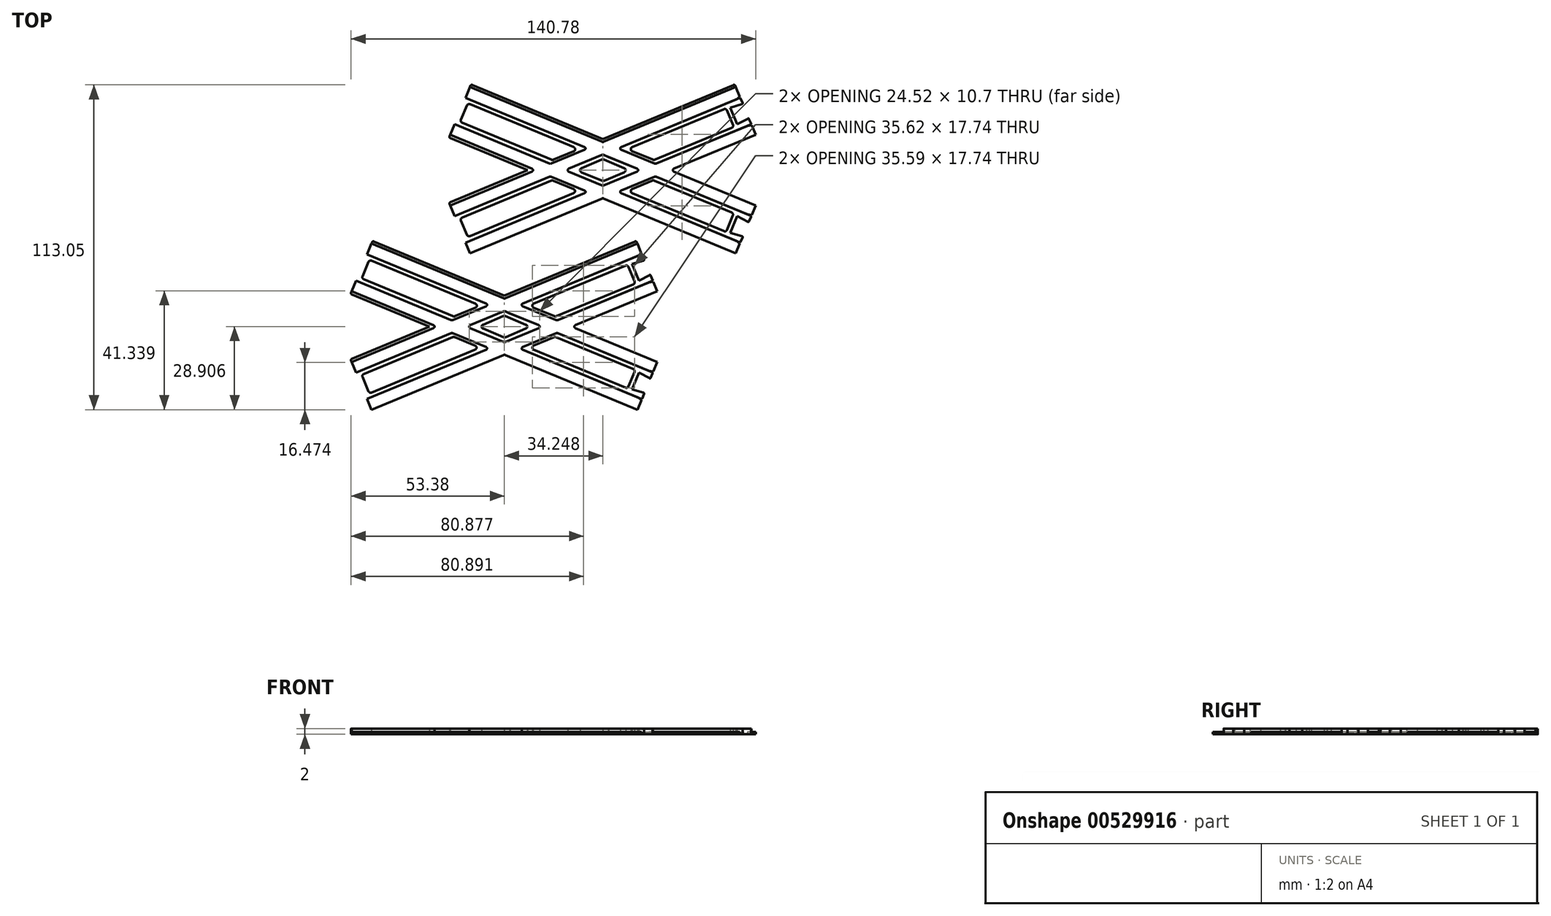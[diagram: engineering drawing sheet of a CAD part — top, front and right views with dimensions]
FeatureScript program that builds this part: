
annotation { "Feature Type Name" : "Feature", "Feature Type Description" : "" }
export const myFeature = defineFeature(function(context is Context, id is Id, definition is map)
    precondition{}
    {
        {
            var Q0;
            Q0=qCreatedBy(makeId("Top.planeOp"),FACE);
            var sketch = newSketch(context, id + "F0", { "sketchPlane" : qUnion([Q0])});
            skLineSegment(sketch, "E0.bottom", {"start": v(-69.8, -34.46) * mm, "end": v(-42.86, -23.3) * mm});
            skLineSegment(sketch, "E0.top", {"start": v(-62.15, -52.94) * mm, "end": v(-16.73, -34.13) * mm});
            skLineSegment(sketch, "E0.left", {"start": v(-70.07, -35.12) * mm, "end": v(-67.43, -41.5) * mm});
            skLineSegment(sketch, "E0.right", {"start": v(29.34, 6.06) * mm, "end": v(30.9, 2.27) * mm});
            skLineSegment(sketch, "E1.bottom", {"start": v(-69.88, -35.58) * mm, "end": v(-41.36, -23.77) * mm});
            skLineSegment(sketch, "E1.left", {"start": v(-69.88, -35.58) * mm, "end": v(-70.07, -35.12) * mm});
            skLineSegment(sketch, "E1.right", {"start": v(29.53, 5.6) * mm, "end": v(29.34, 6.06) * mm});
            skLineSegment(sketch, "E2.top", {"start": v(-63, -52.2) * mm, "end": v(-17.02, -33.16) * mm});
            skLineSegment(sketch, "E2.left", {"start": v(-62.8, -52.67) * mm, "end": v(-63, -52.2) * mm});
            skLineSegment(sketch, "E2.right", {"start": v(36.61, -11.5) * mm, "end": v(36.42, -11.03) * mm});
            skLineSegment(sketch, "E3.top", {"start": v(-68.35, -39.27) * mm, "end": v(-35.3, -25.59) * mm});
            skLineSegment(sketch, "E3.left", {"start": v(-69.88, -35.58) * mm, "end": v(-68.35, -39.27) * mm});
            skLineSegment(sketch, "E3.right", {"start": v(29.53, 5.6) * mm, "end": v(30.9, 2.27) * mm});
            skLineSegment(sketch, "E4.top", {"start": v(-64.52, -48.51) * mm, "end": v(-23.07, -31.34) * mm});
            skLineSegment(sketch, "E4.left", {"start": v(-63, -52.2) * mm, "end": v(-64.52, -48.51) * mm});
            skLineSegment(sketch, "E4.right", {"start": v(36.42, -11.03) * mm, "end": v(35.04, -7.7) * mm});
            skLineSegment(sketch, "E5", {"start": v(-69.59, -45.2) * mm, "end": v(-70.58, -45.07) * mm});
            skLineSegment(sketch, "E6", {"start": v(-70.58, -45.07) * mm, "end": v(-71.45, -42.97) * mm});
            skLineSegment(sketch, "E7", {"start": v(-71.29, -42.63) * mm, "end": v(-67.43, -41.5) * mm});
            skLineSegment(sketch, "E8.MirrorCS", {"start": v(-68.97, -48.21) * mm, "end": v(-65.44, -46.3) * mm});
            skLineSegment(sketch, "E9.MirrorCS", {"start": v(-70.2, -46) * mm, "end": v(-69.32, -48.09) * mm});
            skLineSegment(sketch, "E10.MirrorCS", {"start": v(-69.59, -45.2) * mm, "end": v(-70.2, -46) * mm});
            skLineSegment(sketch, "E11", {"start": v(27.63, -1.52) * mm, "end": v(31.68, -0.3) * mm});
            skLineSegment(sketch, "E12.MirrorCS", {"start": v(30.04, -7.34) * mm, "end": v(33.76, -5.34) * mm});
            skLineSegment(sketch, "E13", {"start": v(27.63, -1.52) * mm, "end": v(30.04, -7.34) * mm});
            skLineSegment(sketch, "E14.trimOffspring", {"start": v(35.04, -7.7) * mm, "end": v(36.61, -11.5) * mm});
            skLineSegment(sketch, "E15", {"start": v(31.16, 1.67) * mm, "end": v(31.84, 0.03) * mm});
            skLineSegment(sketch, "E16", {"start": v(34.11, -5.47) * mm, "end": v(34.89, -7.33) * mm});
            skLineSegment(sketch, "E17.trimOffspring", {"start": v(-65.44, -46.3) * mm, "end": v(-62.8, -52.67) * mm});
            skLineSegment(sketch, "E18", {"start": v(30.9, 2.27) * mm, "end": v(29.68, 1.33) * mm});
            skLineSegment(sketch, "E19", {"start": v(35.04, -7.7) * mm, "end": v(33.5, -7.9) * mm});
            skLineSegment(sketch, "E20.bottom", {"start": v(-65.7, -39.8) * mm, "end": v(-34.75, -26.98) * mm});
            skLineSegment(sketch, "E20.top", {"start": v(-63.02, -46.26) * mm, "end": v(-26.9, -31.3) * mm});
            skLineSegment(sketch, "E20.left", {"start": v(-66.1, -40.78) * mm, "end": v(-64, -45.86) * mm});
            skLineSegment(sketch, "E20.right", {"start": v(26.4, -2.46) * mm, "end": v(28.53, -7.61) * mm});
            skLineSegment(sketch, "E21.bottom", {"start": v(-62.15, 6.33) * mm, "end": v(-16.73, -12.48) * mm});
            skLineSegment(sketch, "E21.top", {"start": v(-69.8, -12.15) * mm, "end": v(-42.86, -23.3) * mm});
            skLineSegment(sketch, "E21.left", {"start": v(-62.8, 6.06) * mm, "end": v(-65.44, -0.31) * mm});
            skLineSegment(sketch, "E21.right", {"start": v(36.61, -35.12) * mm, "end": v(35.04, -38.9) * mm});
            skLineSegment(sketch, "E22.bottom", {"start": v(-63, 5.6) * mm, "end": v(-17.02, -13.44) * mm});
            skLineSegment(sketch, "E22.left", {"start": v(-63, 5.6) * mm, "end": v(-62.8, 6.06) * mm});
            skLineSegment(sketch, "E22.right", {"start": v(36.42, -35.58) * mm, "end": v(36.61, -35.12) * mm});
            skLineSegment(sketch, "E23.top", {"start": v(-69.88, -11.03) * mm, "end": v(-41.36, -22.84) * mm});
            skLineSegment(sketch, "E23.left", {"start": v(-70.07, -11.5) * mm, "end": v(-69.88, -11.03) * mm});
            skLineSegment(sketch, "E23.right", {"start": v(29.34, -52.67) * mm, "end": v(29.53, -52.2) * mm});
            skLineSegment(sketch, "E24.top", {"start": v(-64.52, 1.9) * mm, "end": v(-23.07, -15.27) * mm});
            skLineSegment(sketch, "E24.left", {"start": v(-63, 5.6) * mm, "end": v(-64.52, 1.9) * mm});
            skLineSegment(sketch, "E24.right", {"start": v(36.42, -35.58) * mm, "end": v(35.04, -38.9) * mm});
            skLineSegment(sketch, "E25.top", {"start": v(-68.35, -7.33) * mm, "end": v(-35.3, -21.02) * mm});
            skLineSegment(sketch, "E25.left", {"start": v(-69.88, -11.03) * mm, "end": v(-68.35, -7.33) * mm});
            skLineSegment(sketch, "E25.right", {"start": v(29.53, -52.2) * mm, "end": v(30.9, -48.88) * mm});
            skLineSegment(sketch, "E26", {"start": v(-69.59, -1.41) * mm, "end": v(-70.2, -0.62) * mm});
            skLineSegment(sketch, "E27", {"start": v(-70.2, -0.62) * mm, "end": v(-69.32, 1.48) * mm});
            skLineSegment(sketch, "E28", {"start": v(-68.97, 1.6) * mm, "end": v(-65.44, -0.31) * mm});
            skLineSegment(sketch, "E29.MirrorCS", {"start": v(-71.29, -3.98) * mm, "end": v(-67.43, -5.12) * mm});
            skLineSegment(sketch, "E30.MirrorCS", {"start": v(-70.58, -1.54) * mm, "end": v(-71.45, -3.64) * mm});
            skLineSegment(sketch, "E31.MirrorCS", {"start": v(-69.59, -1.41) * mm, "end": v(-70.58, -1.54) * mm});
            skLineSegment(sketch, "E32", {"start": v(30.04, -39.27) * mm, "end": v(33.76, -41.27) * mm});
            skLineSegment(sketch, "E33.MirrorCS", {"start": v(27.63, -45.09) * mm, "end": v(31.68, -46.3) * mm});
            skLineSegment(sketch, "E34", {"start": v(30.04, -39.27) * mm, "end": v(27.63, -45.09) * mm});
            skLineSegment(sketch, "E35.trimOffspring", {"start": v(30.9, -48.88) * mm, "end": v(29.34, -52.67) * mm});
            skLineSegment(sketch, "E36", {"start": v(34.8, -39.5) * mm, "end": v(34.11, -41.14) * mm});
            skLineSegment(sketch, "E37", {"start": v(31.84, -46.64) * mm, "end": v(31.16, -48.28) * mm});
            skLineSegment(sketch, "E38.trimOffspring", {"start": v(-67.43, -5.12) * mm, "end": v(-70.07, -11.5) * mm});
            skLineSegment(sketch, "E39", {"start": v(35.04, -38.9) * mm, "end": v(33.5, -38.7) * mm});
            skLineSegment(sketch, "E40", {"start": v(30.9, -48.88) * mm, "end": v(29.68, -47.94) * mm});
            skLineSegment(sketch, "E41.bottom", {"start": v(-63.02, -0.34) * mm, "end": v(-26.8, -15.34) * mm});
            skLineSegment(sketch, "E41.top", {"start": v(-65.7, -6.81) * mm, "end": v(-34.66, -19.67) * mm});
            skLineSegment(sketch, "E41.left", {"start": v(-64, -0.75) * mm, "end": v(-66.1, -5.83) * mm});
            skLineSegment(sketch, "E41.right", {"start": v(28.5, -39.06) * mm, "end": v(26.4, -44.15) * mm});
            skLineSegment(sketch, "E42", {"start": v(-6.56, -16.7) * mm, "end": v(0.62, -19.67) * mm});
            skLineSegment(sketch, "E43", {"start": v(-18.62, -27.88) * mm, "end": v(-18.64, -27.92) * mm});
            skPoint(sketch, "E44", {"position": v(-18.64, -18.68) * mm});
            skLineSegment(sketch, "E45.trimOffspring", {"start": v(-16.73, -34.13) * mm, "end": v(28.69, -52.94) * mm});
            skLineSegment(sketch, "E46.trimOffspring", {"start": v(-16.44, -33.16) * mm, "end": v(29.53, -52.2) * mm});
            skLineSegment(sketch, "E47.trimOffspring", {"start": v(-10.39, -31.34) * mm, "end": v(30.83, -48.42) * mm});
            skLineSegment(sketch, "E48.trimOffspring", {"start": v(-6.56, -31.3) * mm, "end": v(25.42, -44.55) * mm});
            skLineSegment(sketch, "E49.trimOffspring", {"start": v(-34.37, -26.82) * mm, "end": v(-26.9, -29.92) * mm});
            skLineSegment(sketch, "E50.trimOffspring", {"start": v(-34.73, -25.59) * mm, "end": v(-23.07, -30.42) * mm});
            skLineSegment(sketch, "E51.trimOffspring", {"start": v(-33.99, -26.98) * mm, "end": v(-26.9, -29.92) * mm});
            skLineSegment(sketch, "E52.trimOffspring", {"start": v(-28.68, -23.77) * mm, "end": v(-17.02, -28.6) * mm});
            skLineSegment(sketch, "E53.trimOffspring", {"start": v(-24.2, -24) * mm, "end": v(-17.02, -26.97) * mm});
            skLineSegment(sketch, "E54.trimOffspring", {"start": v(-16.35, -19.67) * mm, "end": v(-9.26, -22.61) * mm});
            skLineSegment(sketch, "E55.trimOffspring", {"start": v(-16.44, -18.01) * mm, "end": v(-4.78, -22.84) * mm});
            skLineSegment(sketch, "E56.trimOffspring", {"start": v(-23.92, -16.54) * mm, "end": v(-23.07, -16.19) * mm});
            skLineSegment(sketch, "E57.trimOffspring", {"start": v(-18.69, -18.7) * mm, "end": v(-17.02, -18.01) * mm});
            skLineSegment(sketch, "E58.trimOffspring", {"start": v(-14.84, -18.73) * mm, "end": v(-14.77, -18.7) * mm});
            skLineSegment(sketch, "E59.trimOffspring", {"start": v(-5.62, -24.12) * mm, "end": v(-4.78, -23.77) * mm});
            skLineSegment(sketch, "E60.trimOffspring", {"start": v(-0.4, -26.28) * mm, "end": v(1.28, -25.59) * mm});
            skLineSegment(sketch, "E61.trimOffspring", {"start": v(-14.82, -18.68) * mm, "end": v(-14.84, -18.73) * mm});
            skLineSegment(sketch, "E62.trimOffspring", {"start": v(-6.56, -16.7) * mm, "end": v(1, -19.83) * mm});
            skLineSegment(sketch, "E63.trimOffspring", {"start": v(-10.39, -16.19) * mm, "end": v(1.28, -21.02) * mm});
            skLineSegment(sketch, "E64.trimOffspring", {"start": v(1.2, -26.94) * mm, "end": v(28.1, -38.08) * mm});
            skLineSegment(sketch, "E65.trimOffspring", {"start": v(1.85, -25.59) * mm, "end": v(34.66, -39.18) * mm});
            skLineSegment(sketch, "E66.trimOffspring", {"start": v(7.9, -23.77) * mm, "end": v(36.42, -35.58) * mm});
            skLineSegment(sketch, "E67.trimOffspring", {"start": v(9.4, -23.3) * mm, "end": v(36.34, -34.46) * mm});
            skLineSegment(sketch, "E68.trimOffspring", {"start": v(-34.73, -21.02) * mm, "end": v(-33.06, -20.33) * mm});
            skLineSegment(sketch, "E69.trimOffspring", {"start": v(-28.68, -22.84) * mm, "end": v(-27.84, -22.5) * mm});
            skLineSegment(sketch, "E70.trimOffspring", {"start": v(-16.73, -12.48) * mm, "end": v(28.69, 6.33) * mm});
            skLineSegment(sketch, "E71.trimOffspring", {"start": v(-16.44, -13.44) * mm, "end": v(29.53, 5.6) * mm});
            skLineSegment(sketch, "E72.trimOffspring", {"start": v(-10.39, -15.27) * mm, "end": v(30.83, 1.8) * mm});
            skLineSegment(sketch, "E73.trimOffspring", {"start": v(-6.56, -15.3) * mm, "end": v(25.42, -2.06) * mm});
            skLineSegment(sketch, "E74.trimOffspring", {"start": v(-16.44, -28.6) * mm, "end": v(-14.77, -27.9) * mm});
            skLineSegment(sketch, "E75.trimOffspring", {"start": v(1.39, -19.67) * mm, "end": v(28.13, -8.6) * mm});
            skLineSegment(sketch, "E76.trimOffspring", {"start": v(1.85, -21.02) * mm, "end": v(34.89, -7.33) * mm});
            skLineSegment(sketch, "E77.trimOffspring", {"start": v(7.9, -22.84) * mm, "end": v(36.42, -11.03) * mm});
            skLineSegment(sketch, "E78.trimOffspring", {"start": v(9.4, -23.3) * mm, "end": v(36.34, -12.15) * mm});
            skLineSegment(sketch, "E79.trimOffspring", {"start": v(-10.39, -30.42) * mm, "end": v(-9.54, -30.07) * mm});
            skLineSegment(sketch, "E80", {"start": v(-33.06, -20.33) * mm, "end": v(-23.92, -16.54) * mm});
            skLineSegment(sketch, "E81", {"start": v(-27.84, -22.5) * mm, "end": v(-18.64, -18.68) * mm});
            skLineSegment(sketch, "E82", {"start": v(-14.77, -27.9) * mm, "end": v(-5.62, -24.12) * mm});
            skLineSegment(sketch, "E83", {"start": v(-9.54, -30.07) * mm, "end": v(-0.4, -26.28) * mm});
            skLineSegment(sketch, "E84", {"start": v(-24.2, -22.61) * mm, "end": v(-17.11, -19.67) * mm});
            skLineSegment(sketch, "E85", {"start": v(-16.24, -26.97) * mm, "end": v(-9.25, -24) * mm});
            skLineSegment(sketch, "E86", {"start": v(-26.8, -16.73) * mm, "end": v(-33.9, -19.67) * mm});
            skLineSegment(sketch, "E87", {"start": v(-6.57, -29.92) * mm, "end": v(0.42, -26.94) * mm});
            skPoint(sketch, "E88.visualSharp", {"position": v(-40.25, -23.3) * mm});
            skArc(sketch, "E88.filletArc", {"start": v(-41.36, -23.77) * mm, "mid": v(-41.05, -23.3) * mm, "end": v(-41.36, -22.84) * mm});
            skPoint(sketch, "E89.visualSharp", {"position": v(-29.8, -23.3) * mm});
            skArc(sketch, "E89.filletArc", {"start": v(-28.68, -22.84) * mm, "mid": v(-28.99, -23.3) * mm, "end": v(-28.68, -23.77) * mm});
            skPoint(sketch, "E90.visualSharp", {"position": v(-21.96, -15.73) * mm});
            skArc(sketch, "E90.filletArc", {"start": v(-23.07, -16.19) * mm, "mid": v(-22.76, -15.73) * mm, "end": v(-23.07, -15.27) * mm});
            skPoint(sketch, "E91.visualSharp", {"position": v(-3.66, -23.3) * mm});
            skArc(sketch, "E91.filletArc", {"start": v(-4.78, -23.77) * mm, "mid": v(-4.47, -23.3) * mm, "end": v(-4.78, -22.84) * mm});
            skPoint(sketch, "E92.visualSharp", {"position": v(-11.5, -15.73) * mm});
            skArc(sketch, "E92.filletArc", {"start": v(-10.39, -15.27) * mm, "mid": v(-10.7, -15.73) * mm, "end": v(-10.39, -16.19) * mm});
            skPoint(sketch, "E93.visualSharp", {"position": v(6.79, -23.3) * mm});
            skArc(sketch, "E93.filletArc", {"start": v(7.9, -22.84) * mm, "mid": v(7.6, -23.3) * mm, "end": v(7.9, -23.77) * mm});
            skPoint(sketch, "E94.visualSharp", {"position": v(-11.5, -30.88) * mm});
            skArc(sketch, "E94.filletArc", {"start": v(-10.39, -30.42) * mm, "mid": v(-10.7, -30.88) * mm, "end": v(-10.39, -31.34) * mm});
            skPoint(sketch, "E95.visualSharp", {"position": v(-21.96, -30.88) * mm});
            skArc(sketch, "E95.filletArc", {"start": v(-23.07, -31.34) * mm, "mid": v(-22.76, -30.88) * mm, "end": v(-23.07, -30.42) * mm});
            skPoint(sketch, "E96.visualSharp", {"position": v(-16.73, -33.05) * mm});
            skArc(sketch, "E96.filletArc", {"start": v(-16.44, -33.16) * mm, "mid": v(-16.73, -33.1) * mm, "end": v(-17.02, -33.16) * mm});
            skPoint(sketch, "E97.visualSharp", {"position": v(1.56, -21.14) * mm});
            skArc(sketch, "E97.filletArc", {"start": v(1.28, -21.02) * mm, "mid": v(1.56, -21.08) * mm, "end": v(1.85, -21.02) * mm});
            skPoint(sketch, "E98.visualSharp", {"position": v(1.56, -25.47) * mm});
            skArc(sketch, "E98.filletArc", {"start": v(1.85, -25.59) * mm, "mid": v(1.56, -25.53) * mm, "end": v(1.28, -25.59) * mm});
            skPoint(sketch, "E99.visualSharp", {"position": v(-16.73, -28.72) * mm});
            skArc(sketch, "E99.filletArc", {"start": v(-17.02, -28.6) * mm, "mid": v(-16.73, -28.65) * mm, "end": v(-16.44, -28.6) * mm});
            skPoint(sketch, "E100.visualSharp", {"position": v(-16.73, -17.9) * mm});
            skArc(sketch, "E100.filletArc", {"start": v(-16.44, -18.01) * mm, "mid": v(-16.73, -17.95) * mm, "end": v(-17.02, -18.01) * mm});
            skPoint(sketch, "E101.visualSharp", {"position": v(-16.73, -13.56) * mm});
            skArc(sketch, "E101.filletArc", {"start": v(-17.02, -13.44) * mm, "mid": v(-16.73, -13.5) * mm, "end": v(-16.44, -13.44) * mm});
            skPoint(sketch, "E102.visualSharp", {"position": v(-35.02, -21.14) * mm});
            skArc(sketch, "E102.filletArc", {"start": v(-35.3, -21.02) * mm, "mid": v(-35.02, -21.08) * mm, "end": v(-34.73, -21.02) * mm});
            skPoint(sketch, "E103.visualSharp", {"position": v(-35.02, -25.47) * mm});
            skArc(sketch, "E103.filletArc", {"start": v(-34.73, -25.59) * mm, "mid": v(-35.02, -25.53) * mm, "end": v(-35.3, -25.59) * mm});
            skPoint(sketch, "E104.visualSharp", {"position": v(-70.26, -11.95) * mm});
            skArc(sketch, "E104.filletArc", {"start": v(-70.07, -11.5) * mm, "mid": v(-70.07, -11.87) * mm, "end": v(-69.8, -12.15) * mm});
            skPoint(sketch, "E105.visualSharp", {"position": v(-62.6, 6.52) * mm});
            skArc(sketch, "E105.filletArc", {"start": v(-62.15, 6.33) * mm, "mid": v(-62.53, 6.33) * mm, "end": v(-62.8, 6.06) * mm});
            skPoint(sketch, "E106.visualSharp", {"position": v(-69.22, 1.74) * mm});
            skArc(sketch, "E106.filletArc", {"start": v(-68.97, 1.6) * mm, "mid": v(-69.18, 1.62) * mm, "end": v(-69.32, 1.48) * mm});
            skPoint(sketch, "E107.visualSharp", {"position": v(-71.55, -3.9) * mm});
            skArc(sketch, "E107.filletArc", {"start": v(-71.45, -3.64) * mm, "mid": v(-71.44, -3.84) * mm, "end": v(-71.29, -3.98) * mm});
            skPoint(sketch, "E108.visualSharp", {"position": v(-66.39, -6.52) * mm});
            skArc(sketch, "E108.filletArc", {"start": v(-66.1, -5.83) * mm, "mid": v(-66.1, -6.4) * mm, "end": v(-65.7, -6.81) * mm});
            skPoint(sketch, "E109.visualSharp", {"position": v(-63.7, -0.06) * mm});
            skArc(sketch, "E109.filletArc", {"start": v(-63.02, -0.34) * mm, "mid": v(-63.6, -0.34) * mm, "end": v(-64, -0.75) * mm});
            skPoint(sketch, "E110.visualSharp", {"position": v(31.94, -0.22) * mm});
            skArc(sketch, "E110.filletArc", {"start": v(31.68, -0.3) * mm, "mid": v(31.83, -0.17) * mm, "end": v(31.84, 0.03) * mm});
            skPoint(sketch, "E111.visualSharp", {"position": v(34, -5.2) * mm});
            skArc(sketch, "E111.filletArc", {"start": v(34.11, -5.47) * mm, "mid": v(33.97, -5.33) * mm, "end": v(33.76, -5.34) * mm});
            skPoint(sketch, "E112.visualSharp", {"position": v(29.15, 6.52) * mm});
            skArc(sketch, "E112.filletArc", {"start": v(29.34, 6.06) * mm, "mid": v(29.07, 6.33) * mm, "end": v(28.69, 6.33) * mm});
            skPoint(sketch, "E113.visualSharp", {"position": v(36.8, -11.95) * mm});
            skArc(sketch, "E113.filletArc", {"start": v(36.34, -12.15) * mm, "mid": v(36.61, -11.87) * mm, "end": v(36.61, -11.5) * mm});
            skPoint(sketch, "E114.visualSharp", {"position": v(36.8, -34.65) * mm});
            skArc(sketch, "E114.filletArc", {"start": v(36.61, -35.12) * mm, "mid": v(36.61, -34.73) * mm, "end": v(36.34, -34.46) * mm});
            skPoint(sketch, "E115.visualSharp", {"position": v(29.15, -53.13) * mm});
            skArc(sketch, "E115.filletArc", {"start": v(28.69, -52.94) * mm, "mid": v(29.07, -52.94) * mm, "end": v(29.34, -52.67) * mm});
            skPoint(sketch, "E116.visualSharp", {"position": v(31.06, -48.51) * mm});
            skArc(sketch, "E116.filletArc", {"start": v(30.83, -48.42) * mm, "mid": v(31.02, -48.42) * mm, "end": v(31.16, -48.28) * mm});
            skPoint(sketch, "E117.visualSharp", {"position": v(34.89, -39.27) * mm});
            skArc(sketch, "E117.filletArc", {"start": v(34.8, -39.5) * mm, "mid": v(34.8, -39.31) * mm, "end": v(34.66, -39.18) * mm});
            skPoint(sketch, "E118.visualSharp", {"position": v(34, -41.4) * mm});
            skArc(sketch, "E118.filletArc", {"start": v(33.76, -41.27) * mm, "mid": v(33.97, -41.28) * mm, "end": v(34.11, -41.14) * mm});
            skPoint(sketch, "E119.visualSharp", {"position": v(31.94, -46.39) * mm});
            skArc(sketch, "E119.filletArc", {"start": v(31.84, -46.64) * mm, "mid": v(31.83, -46.44) * mm, "end": v(31.68, -46.3) * mm});
            skPoint(sketch, "E120.visualSharp", {"position": v(26.11, -44.84) * mm});
            skArc(sketch, "E120.filletArc", {"start": v(25.42, -44.55) * mm, "mid": v(26, -44.55) * mm, "end": v(26.4, -44.15) * mm});
            skPoint(sketch, "E121.visualSharp", {"position": v(28.8, -38.37) * mm});
            skArc(sketch, "E121.filletArc", {"start": v(28.5, -39.06) * mm, "mid": v(28.5, -38.49) * mm, "end": v(28.1, -38.08) * mm});
            skPoint(sketch, "E122.visualSharp", {"position": v(-8.21, -30.62) * mm});
            skArc(sketch, "E122.filletArc", {"start": v(-6.57, -29.92) * mm, "mid": v(-7.03, -30.61) * mm, "end": v(-6.56, -31.3) * mm});
            skPoint(sketch, "E123.visualSharp", {"position": v(0.8, -26.78) * mm});
            skArc(sketch, "E123.filletArc", {"start": v(1.2, -26.94) * mm, "mid": v(0.8, -26.86) * mm, "end": v(0.42, -26.94) * mm});
            skPoint(sketch, "E124.visualSharp", {"position": v(-25.88, -23.3) * mm});
            skArc(sketch, "E124.filletArc", {"start": v(-24.2, -22.61) * mm, "mid": v(-24.67, -23.3) * mm, "end": v(-24.2, -24) * mm});
            skPoint(sketch, "E125.visualSharp", {"position": v(-7.6, -23.3) * mm});
            skArc(sketch, "E125.filletArc", {"start": v(-9.25, -24) * mm, "mid": v(-8.8, -23.3) * mm, "end": v(-9.26, -22.61) * mm});
            skPoint(sketch, "E126.visualSharp", {"position": v(-8.24, -16) * mm});
            skArc(sketch, "E126.filletArc", {"start": v(-6.56, -15.3) * mm, "mid": v(-7.03, -16) * mm, "end": v(-6.56, -16.7) * mm});
            skPoint(sketch, "E127.visualSharp", {"position": v(-25.22, -30.6) * mm});
            skArc(sketch, "E127.filletArc", {"start": v(-26.9, -31.3) * mm, "mid": v(-26.43, -30.6) * mm, "end": v(-26.9, -29.92) * mm});
            skPoint(sketch, "E128.visualSharp", {"position": v(-63.7, -46.55) * mm});
            skArc(sketch, "E128.filletArc", {"start": v(-64, -45.86) * mm, "mid": v(-63.6, -46.26) * mm, "end": v(-63.02, -46.26) * mm});
            skPoint(sketch, "E129.visualSharp", {"position": v(-66.39, -40.08) * mm});
            skArc(sketch, "E129.filletArc", {"start": v(-65.7, -39.8) * mm, "mid": v(-66.1, -40.2) * mm, "end": v(-66.1, -40.78) * mm});
            skPoint(sketch, "E130.visualSharp", {"position": v(-71.55, -42.71) * mm});
            skArc(sketch, "E130.filletArc", {"start": v(-71.29, -42.63) * mm, "mid": v(-71.44, -42.76) * mm, "end": v(-71.45, -42.97) * mm});
            skPoint(sketch, "E131.visualSharp", {"position": v(-69.22, -48.35) * mm});
            skArc(sketch, "E131.filletArc", {"start": v(-69.32, -48.09) * mm, "mid": v(-69.18, -48.23) * mm, "end": v(-68.97, -48.21) * mm});
            skPoint(sketch, "E132.visualSharp", {"position": v(-70.26, -34.65) * mm});
            skArc(sketch, "E132.filletArc", {"start": v(-69.8, -34.46) * mm, "mid": v(-70.07, -34.73) * mm, "end": v(-70.07, -35.12) * mm});
            skPoint(sketch, "E133.visualSharp", {"position": v(-62.6, -53.13) * mm});
            skArc(sketch, "E133.filletArc", {"start": v(-62.8, -52.67) * mm, "mid": v(-62.53, -52.94) * mm, "end": v(-62.15, -52.94) * mm});
            skPoint(sketch, "E134.visualSharp", {"position": v(-34.37, -26.82) * mm});
            skArc(sketch, "E134.filletArc", {"start": v(-33.99, -26.98) * mm, "mid": v(-34.37, -26.9) * mm, "end": v(-34.75, -26.98) * mm});
            skPoint(sketch, "E135.visualSharp", {"position": v(-16.63, -27.13) * mm});
            skArc(sketch, "E135.filletArc", {"start": v(-17.02, -26.97) * mm, "mid": v(-16.63, -27.05) * mm, "end": v(-16.24, -26.97) * mm});
            skPoint(sketch, "E136.visualSharp", {"position": v(-16.73, -19.52) * mm});
            skArc(sketch, "E136.filletArc", {"start": v(-16.35, -19.67) * mm, "mid": v(-16.73, -19.6) * mm, "end": v(-17.11, -19.67) * mm});
            skPoint(sketch, "E137.visualSharp", {"position": v(1, -19.83) * mm});
            skArc(sketch, "E137.filletArc", {"start": v(0.62, -19.67) * mm, "mid": v(1, -19.74) * mm, "end": v(1.39, -19.67) * mm});
            skPoint(sketch, "E138.visualSharp", {"position": v(26.11, -1.77) * mm});
            skArc(sketch, "E138.filletArc", {"start": v(26.4, -2.46) * mm, "mid": v(26, -2.06) * mm, "end": v(25.42, -2.06) * mm});
            skPoint(sketch, "E139.visualSharp", {"position": v(28.82, -8.3) * mm});
            skArc(sketch, "E139.filletArc", {"start": v(28.13, -8.6) * mm, "mid": v(28.53, -8.19) * mm, "end": v(28.53, -7.61) * mm});
            skPoint(sketch, "E140.visualSharp", {"position": v(-34.27, -19.83) * mm});
            skArc(sketch, "E140.filletArc", {"start": v(-34.66, -19.67) * mm, "mid": v(-34.27, -19.74) * mm, "end": v(-33.9, -19.67) * mm});
            skPoint(sketch, "E141.visualSharp", {"position": v(-25.13, -16.04) * mm});
            skArc(sketch, "E141.filletArc", {"start": v(-26.8, -16.73) * mm, "mid": v(-26.34, -16.04) * mm, "end": v(-26.8, -15.34) * mm});
            skPoint(sketch, "E142.visualSharp", {"position": v(31.06, 1.9) * mm});
            skArc(sketch, "E142.filletArc", {"start": v(31.16, 1.67) * mm, "mid": v(31.02, 1.8) * mm, "end": v(30.83, 1.8) * mm});
            skLineSegment(sketch, "E143.bottom", {"start": v(-35.55, 20.01) * mm, "end": v(-8.61, 31.17) * mm});
            skLineSegment(sketch, "E143.top", {"start": v(-27.9, 1.53) * mm, "end": v(17.52, 20.35) * mm});
            skLineSegment(sketch, "E143.left", {"start": v(-35.82, 19.36) * mm, "end": v(-33.18, 12.98) * mm});
            skLineSegment(sketch, "E143.right", {"start": v(63.59, 60.53) * mm, "end": v(65.16, 56.75) * mm});
            skLineSegment(sketch, "E144.bottom", {"start": v(-35.63, 18.9) * mm, "end": v(-7.11, 30.7) * mm});
            skLineSegment(sketch, "E144.left", {"start": v(-35.63, 18.9) * mm, "end": v(-35.82, 19.36) * mm});
            skLineSegment(sketch, "E144.right", {"start": v(63.78, 60.07) * mm, "end": v(63.59, 60.53) * mm});
            skLineSegment(sketch, "E145.top", {"start": v(-28.74, 2.27) * mm, "end": v(17.23, 21.3) * mm});
            skLineSegment(sketch, "E145.left", {"start": v(-28.55, 1.8) * mm, "end": v(-28.74, 2.27) * mm});
            skLineSegment(sketch, "E145.right", {"start": v(70.86, 42.98) * mm, "end": v(70.67, 43.44) * mm});
            skLineSegment(sketch, "E146.top", {"start": v(-34.1, 15.2) * mm, "end": v(-1.06, 28.89) * mm});
            skLineSegment(sketch, "E146.left", {"start": v(-35.63, 18.9) * mm, "end": v(-34.1, 15.2) * mm});
            skLineSegment(sketch, "E146.right", {"start": v(63.78, 60.07) * mm, "end": v(65.16, 56.75) * mm});
            skLineSegment(sketch, "E147.top", {"start": v(-30.27, 5.96) * mm, "end": v(11.18, 23.13) * mm});
            skLineSegment(sketch, "E147.left", {"start": v(-28.74, 2.27) * mm, "end": v(-30.27, 5.96) * mm});
            skLineSegment(sketch, "E147.right", {"start": v(70.67, 43.44) * mm, "end": v(69.29, 46.77) * mm});
            skLineSegment(sketch, "E148", {"start": v(-35.34, 9.28) * mm, "end": v(-36.33, 9.4) * mm});
            skLineSegment(sketch, "E149", {"start": v(-36.33, 9.4) * mm, "end": v(-37.2, 11.5) * mm});
            skLineSegment(sketch, "E150", {"start": v(-37.04, 11.84) * mm, "end": v(-33.18, 12.98) * mm});
            skLineSegment(sketch, "E151.MirrorCS", {"start": v(-34.73, 6.26) * mm, "end": v(-31.2, 8.18) * mm});
            skLineSegment(sketch, "E152.MirrorCS", {"start": v(-35.95, 8.48) * mm, "end": v(-35.08, 6.38) * mm});
            skLineSegment(sketch, "E153.MirrorCS", {"start": v(-35.34, 9.28) * mm, "end": v(-35.95, 8.48) * mm});
            skLineSegment(sketch, "E154", {"start": v(61.88, 52.95) * mm, "end": v(65.93, 54.17) * mm});
            skLineSegment(sketch, "E155.MirrorCS", {"start": v(64.3, 47.13) * mm, "end": v(68.01, 49.13) * mm});
            skLineSegment(sketch, "E156", {"start": v(61.88, 52.95) * mm, "end": v(64.3, 47.13) * mm});
            skLineSegment(sketch, "E157.trimOffspring", {"start": v(69.29, 46.77) * mm, "end": v(70.86, 42.98) * mm});
            skLineSegment(sketch, "E158", {"start": v(65.4, 56.15) * mm, "end": v(66.08, 54.5) * mm});
            skLineSegment(sketch, "E159", {"start": v(68.36, 49) * mm, "end": v(69.14, 47.14) * mm});
            skLineSegment(sketch, "E160.trimOffspring", {"start": v(-31.2, 8.18) * mm, "end": v(-28.55, 1.8) * mm});
            skLineSegment(sketch, "E161", {"start": v(65.16, 56.75) * mm, "end": v(63.92, 55.8) * mm});
            skLineSegment(sketch, "E162", {"start": v(69.29, 46.77) * mm, "end": v(67.75, 46.56) * mm});
            skLineSegment(sketch, "E163.bottom", {"start": v(-31.45, 14.68) * mm, "end": v(-0.5, 27.5) * mm});
            skLineSegment(sketch, "E163.top", {"start": v(-28.77, 8.2) * mm, "end": v(7.35, 23.17) * mm});
            skLineSegment(sketch, "E163.left", {"start": v(-31.85, 13.7) * mm, "end": v(-29.75, 8.61) * mm});
            skLineSegment(sketch, "E163.right", {"start": v(60.65, 52.01) * mm, "end": v(62.78, 46.86) * mm});
            skLineSegment(sketch, "E164.bottom", {"start": v(-27.9, 60.8) * mm, "end": v(17.52, 42) * mm});
            skLineSegment(sketch, "E164.top", {"start": v(-35.55, 42.33) * mm, "end": v(-8.61, 31.17) * mm});
            skLineSegment(sketch, "E164.left", {"start": v(-28.55, 60.53) * mm, "end": v(-31.2, 54.16) * mm});
            skLineSegment(sketch, "E164.right", {"start": v(70.86, 19.36) * mm, "end": v(69.3, 15.57) * mm});
            skLineSegment(sketch, "E165.bottom", {"start": v(-28.74, 60.07) * mm, "end": v(17.23, 41.03) * mm});
            skLineSegment(sketch, "E165.left", {"start": v(-28.74, 60.07) * mm, "end": v(-28.55, 60.53) * mm});
            skLineSegment(sketch, "E165.right", {"start": v(70.67, 18.9) * mm, "end": v(70.86, 19.36) * mm});
            skLineSegment(sketch, "E166.top", {"start": v(-35.63, 43.44) * mm, "end": v(-7.11, 31.63) * mm});
            skLineSegment(sketch, "E166.left", {"start": v(-35.82, 42.98) * mm, "end": v(-35.63, 43.44) * mm});
            skLineSegment(sketch, "E166.right", {"start": v(63.59, 1.8) * mm, "end": v(63.78, 2.27) * mm});
            skLineSegment(sketch, "E167.top", {"start": v(-30.27, 56.38) * mm, "end": v(11.18, 39.2) * mm});
            skLineSegment(sketch, "E167.left", {"start": v(-28.74, 60.07) * mm, "end": v(-30.27, 56.38) * mm});
            skLineSegment(sketch, "E167.right", {"start": v(70.67, 18.9) * mm, "end": v(69.3, 15.57) * mm});
            skLineSegment(sketch, "E168.top", {"start": v(-34.1, 47.14) * mm, "end": v(-1.06, 33.45) * mm});
            skLineSegment(sketch, "E168.left", {"start": v(-35.63, 43.44) * mm, "end": v(-34.1, 47.14) * mm});
            skLineSegment(sketch, "E168.right", {"start": v(63.78, 2.27) * mm, "end": v(65.16, 5.6) * mm});
            skLineSegment(sketch, "E169", {"start": v(-35.34, 53.06) * mm, "end": v(-35.95, 53.86) * mm});
            skLineSegment(sketch, "E170", {"start": v(-35.95, 53.86) * mm, "end": v(-35.08, 55.96) * mm});
            skLineSegment(sketch, "E171", {"start": v(-34.73, 56.08) * mm, "end": v(-31.2, 54.16) * mm});
            skLineSegment(sketch, "E172.MirrorCS", {"start": v(-37.04, 50.5) * mm, "end": v(-33.18, 49.36) * mm});
            skLineSegment(sketch, "E173.MirrorCS", {"start": v(-36.33, 52.93) * mm, "end": v(-37.2, 50.83) * mm});
            skLineSegment(sketch, "E174.MirrorCS", {"start": v(-35.34, 53.06) * mm, "end": v(-36.33, 52.93) * mm});
            skLineSegment(sketch, "E175", {"start": v(64.3, 15.2) * mm, "end": v(68.01, 13.2) * mm});
            skLineSegment(sketch, "E176.MirrorCS", {"start": v(61.88, 9.38) * mm, "end": v(65.93, 8.17) * mm});
            skLineSegment(sketch, "E177", {"start": v(64.3, 15.2) * mm, "end": v(61.88, 9.38) * mm});
            skLineSegment(sketch, "E178.trimOffspring", {"start": v(65.16, 5.6) * mm, "end": v(63.59, 1.8) * mm});
            skLineSegment(sketch, "E179", {"start": v(69.04, 14.97) * mm, "end": v(68.36, 13.33) * mm});
            skLineSegment(sketch, "E180", {"start": v(66.08, 7.83) * mm, "end": v(65.4, 6.2) * mm});
            skLineSegment(sketch, "E181.trimOffspring", {"start": v(-33.18, 49.36) * mm, "end": v(-35.82, 42.98) * mm});
            skLineSegment(sketch, "E182", {"start": v(69.3, 15.57) * mm, "end": v(67.75, 15.77) * mm});
            skLineSegment(sketch, "E183", {"start": v(65.16, 5.6) * mm, "end": v(63.92, 6.54) * mm});
            skLineSegment(sketch, "E184.bottom", {"start": v(-28.77, 54.13) * mm, "end": v(7.45, 39.13) * mm});
            skLineSegment(sketch, "E184.top", {"start": v(-31.45, 47.66) * mm, "end": v(-0.4, 34.8) * mm});
            skLineSegment(sketch, "E184.left", {"start": v(-29.75, 53.72) * mm, "end": v(-31.85, 48.64) * mm});
            skLineSegment(sketch, "E184.right", {"start": v(62.75, 15.4) * mm, "end": v(60.65, 10.33) * mm});
            skLineSegment(sketch, "E185", {"start": v(27.68, 37.78) * mm, "end": v(34.87, 34.8) * mm});
            skLineSegment(sketch, "E186", {"start": v(15.62, 26.6) * mm, "end": v(15.6, 26.55) * mm});
            skPoint(sketch, "E187", {"position": v(15.6, 35.79) * mm});
            skLineSegment(sketch, "E188.trimOffspring", {"start": v(17.52, 20.35) * mm, "end": v(62.94, 1.53) * mm});
            skLineSegment(sketch, "E189.trimOffspring", {"start": v(17.8, 21.3) * mm, "end": v(63.78, 2.27) * mm});
            skLineSegment(sketch, "E190.trimOffspring", {"start": v(23.86, 23.13) * mm, "end": v(65.08, 6.06) * mm});
            skLineSegment(sketch, "E191.trimOffspring", {"start": v(27.68, 23.17) * mm, "end": v(59.67, 9.92) * mm});
            skLineSegment(sketch, "E192.trimOffspring", {"start": v(-0.12, 27.65) * mm, "end": v(7.35, 24.56) * mm});
            skLineSegment(sketch, "E193.trimOffspring", {"start": v(-0.49, 28.89) * mm, "end": v(11.18, 24.05) * mm});
            skLineSegment(sketch, "E194.trimOffspring", {"start": v(0.26, 27.5) * mm, "end": v(7.35, 24.56) * mm});
            skLineSegment(sketch, "E195.trimOffspring", {"start": v(5.57, 30.7) * mm, "end": v(17.23, 25.88) * mm});
            skLineSegment(sketch, "E196.trimOffspring", {"start": v(10.05, 30.48) * mm, "end": v(17.23, 27.5) * mm});
            skLineSegment(sketch, "E197.trimOffspring", {"start": v(17.9, 34.8) * mm, "end": v(25, 31.86) * mm});
            skLineSegment(sketch, "E198.trimOffspring", {"start": v(17.8, 36.46) * mm, "end": v(29.47, 31.63) * mm});
            skLineSegment(sketch, "E199.trimOffspring", {"start": v(10.33, 37.93) * mm, "end": v(11.18, 38.28) * mm});
            skLineSegment(sketch, "E200.trimOffspring", {"start": v(15.56, 35.77) * mm, "end": v(17.23, 36.46) * mm});
            skLineSegment(sketch, "E201.trimOffspring", {"start": v(19.41, 35.74) * mm, "end": v(19.48, 35.77) * mm});
            skLineSegment(sketch, "E202.trimOffspring", {"start": v(28.62, 30.36) * mm, "end": v(29.47, 30.7) * mm});
            skLineSegment(sketch, "E203.trimOffspring", {"start": v(33.85, 28.2) * mm, "end": v(35.52, 28.89) * mm});
            skLineSegment(sketch, "E204.trimOffspring", {"start": v(19.43, 35.79) * mm, "end": v(19.41, 35.74) * mm});
            skLineSegment(sketch, "E205.trimOffspring", {"start": v(27.68, 37.78) * mm, "end": v(35.25, 34.65) * mm});
            skLineSegment(sketch, "E206.trimOffspring", {"start": v(23.86, 38.28) * mm, "end": v(35.52, 33.45) * mm});
            skLineSegment(sketch, "E207.trimOffspring", {"start": v(35.44, 27.53) * mm, "end": v(62.35, 16.39) * mm});
            skLineSegment(sketch, "E208.trimOffspring", {"start": v(36.1, 28.89) * mm, "end": v(68.9, 15.3) * mm});
            skLineSegment(sketch, "E209.trimOffspring", {"start": v(42.15, 30.7) * mm, "end": v(70.67, 18.9) * mm});
            skLineSegment(sketch, "E210.trimOffspring", {"start": v(43.65, 31.17) * mm, "end": v(70.59, 20.01) * mm});
            skLineSegment(sketch, "E211.trimOffspring", {"start": v(-0.49, 33.45) * mm, "end": v(1.19, 34.15) * mm});
            skLineSegment(sketch, "E212.trimOffspring", {"start": v(5.57, 31.63) * mm, "end": v(6.41, 31.98) * mm});
            skLineSegment(sketch, "E213.trimOffspring", {"start": v(17.52, 42) * mm, "end": v(62.93, 60.8) * mm});
            skLineSegment(sketch, "E214.trimOffspring", {"start": v(17.8, 41.03) * mm, "end": v(63.78, 60.07) * mm});
            skLineSegment(sketch, "E215.trimOffspring", {"start": v(23.86, 39.2) * mm, "end": v(65.08, 56.28) * mm});
            skLineSegment(sketch, "E216.trimOffspring", {"start": v(27.68, 39.17) * mm, "end": v(59.67, 52.42) * mm});
            skLineSegment(sketch, "E217.trimOffspring", {"start": v(17.8, 25.88) * mm, "end": v(19.48, 26.57) * mm});
            skLineSegment(sketch, "E218.trimOffspring", {"start": v(35.64, 34.8) * mm, "end": v(62.38, 45.88) * mm});
            skLineSegment(sketch, "E219.trimOffspring", {"start": v(36.1, 33.45) * mm, "end": v(69.14, 47.14) * mm});
            skLineSegment(sketch, "E220.trimOffspring", {"start": v(42.15, 31.63) * mm, "end": v(70.67, 43.44) * mm});
            skLineSegment(sketch, "E221.trimOffspring", {"start": v(43.65, 31.17) * mm, "end": v(70.59, 42.33) * mm});
            skLineSegment(sketch, "E222.trimOffspring", {"start": v(23.86, 24.05) * mm, "end": v(24.7, 24.4) * mm});
            skLineSegment(sketch, "E223", {"start": v(1.19, 34.15) * mm, "end": v(10.33, 37.93) * mm});
            skLineSegment(sketch, "E224", {"start": v(6.41, 31.98) * mm, "end": v(15.6, 35.79) * mm});
            skLineSegment(sketch, "E225", {"start": v(19.48, 26.57) * mm, "end": v(28.62, 30.36) * mm});
            skLineSegment(sketch, "E226", {"start": v(24.7, 24.4) * mm, "end": v(33.85, 28.2) * mm});
            skLineSegment(sketch, "E227", {"start": v(10.05, 31.86) * mm, "end": v(17.14, 34.8) * mm});
            skLineSegment(sketch, "E228", {"start": v(18, 27.5) * mm, "end": v(25, 30.48) * mm});
            skLineSegment(sketch, "E229", {"start": v(7.45, 37.74) * mm, "end": v(0.36, 34.8) * mm});
            skLineSegment(sketch, "E230", {"start": v(27.68, 24.55) * mm, "end": v(34.67, 27.53) * mm});
            skPoint(sketch, "E231.visualSharp", {"position": v(-6, 31.17) * mm});
            skArc(sketch, "E231.filletArc", {"start": v(-7.11, 30.7) * mm, "mid": v(-6.8, 31.17) * mm, "end": v(-7.11, 31.63) * mm});
            skPoint(sketch, "E232.visualSharp", {"position": v(4.45, 31.17) * mm});
            skArc(sketch, "E232.filletArc", {"start": v(5.57, 31.63) * mm, "mid": v(5.26, 31.17) * mm, "end": v(5.57, 30.7) * mm});
            skPoint(sketch, "E233.visualSharp", {"position": v(12.3, 38.75) * mm});
            skArc(sketch, "E233.filletArc", {"start": v(11.18, 38.28) * mm, "mid": v(11.49, 38.75) * mm, "end": v(11.18, 39.2) * mm});
            skPoint(sketch, "E234.visualSharp", {"position": v(30.58, 31.17) * mm});
            skArc(sketch, "E234.filletArc", {"start": v(29.47, 30.7) * mm, "mid": v(29.78, 31.17) * mm, "end": v(29.47, 31.63) * mm});
            skPoint(sketch, "E235.visualSharp", {"position": v(22.74, 38.75) * mm});
            skArc(sketch, "E235.filletArc", {"start": v(23.86, 39.2) * mm, "mid": v(23.55, 38.75) * mm, "end": v(23.86, 38.28) * mm});
            skPoint(sketch, "E236.visualSharp", {"position": v(41.04, 31.17) * mm});
            skArc(sketch, "E236.filletArc", {"start": v(42.15, 31.63) * mm, "mid": v(41.84, 31.17) * mm, "end": v(42.15, 30.7) * mm});
            skPoint(sketch, "E237.visualSharp", {"position": v(22.74, 23.6) * mm});
            skArc(sketch, "E237.filletArc", {"start": v(23.86, 24.05) * mm, "mid": v(23.55, 23.6) * mm, "end": v(23.86, 23.13) * mm});
            skPoint(sketch, "E238.visualSharp", {"position": v(12.3, 23.6) * mm});
            skArc(sketch, "E238.filletArc", {"start": v(11.18, 23.13) * mm, "mid": v(11.49, 23.6) * mm, "end": v(11.18, 24.05) * mm});
            skPoint(sketch, "E239.visualSharp", {"position": v(17.52, 21.43) * mm});
            skArc(sketch, "E239.filletArc", {"start": v(17.8, 21.3) * mm, "mid": v(17.52, 21.37) * mm, "end": v(17.23, 21.3) * mm});
            skPoint(sketch, "E240.visualSharp", {"position": v(35.81, 33.33) * mm});
            skArc(sketch, "E240.filletArc", {"start": v(35.52, 33.45) * mm, "mid": v(35.81, 33.4) * mm, "end": v(36.1, 33.45) * mm});
            skPoint(sketch, "E241.visualSharp", {"position": v(35.81, 29) * mm});
            skArc(sketch, "E241.filletArc", {"start": v(36.1, 28.89) * mm, "mid": v(35.81, 28.94) * mm, "end": v(35.52, 28.89) * mm});
            skPoint(sketch, "E242.visualSharp", {"position": v(17.52, 25.76) * mm});
            skArc(sketch, "E242.filletArc", {"start": v(17.23, 25.88) * mm, "mid": v(17.52, 25.82) * mm, "end": v(17.8, 25.88) * mm});
            skPoint(sketch, "E243.visualSharp", {"position": v(17.52, 36.58) * mm});
            skArc(sketch, "E243.filletArc", {"start": v(17.8, 36.46) * mm, "mid": v(17.52, 36.52) * mm, "end": v(17.23, 36.46) * mm});
            skPoint(sketch, "E244.visualSharp", {"position": v(17.52, 40.91) * mm});
            skArc(sketch, "E244.filletArc", {"start": v(17.23, 41.03) * mm, "mid": v(17.52, 40.97) * mm, "end": v(17.8, 41.03) * mm});
            skPoint(sketch, "E245.visualSharp", {"position": v(-0.77, 33.33) * mm});
            skArc(sketch, "E245.filletArc", {"start": v(-1.06, 33.45) * mm, "mid": v(-0.77, 33.4) * mm, "end": v(-0.49, 33.45) * mm});
            skPoint(sketch, "E246.visualSharp", {"position": v(-0.77, 29) * mm});
            skArc(sketch, "E246.filletArc", {"start": v(-0.49, 28.89) * mm, "mid": v(-0.77, 28.94) * mm, "end": v(-1.06, 28.89) * mm});
            skPoint(sketch, "E247.visualSharp", {"position": v(-36.01, 42.52) * mm});
            skArc(sketch, "E247.filletArc", {"start": v(-35.82, 42.98) * mm, "mid": v(-35.82, 42.6) * mm, "end": v(-35.55, 42.33) * mm});
            skPoint(sketch, "E248.visualSharp", {"position": v(-28.36, 61) * mm});
            skArc(sketch, "E248.filletArc", {"start": v(-27.9, 60.8) * mm, "mid": v(-28.28, 60.8) * mm, "end": v(-28.55, 60.53) * mm});
            skPoint(sketch, "E249.visualSharp", {"position": v(-34.97, 56.21) * mm});
            skArc(sketch, "E249.filletArc", {"start": v(-34.73, 56.08) * mm, "mid": v(-34.93, 56.1) * mm, "end": v(-35.08, 55.96) * mm});
            skPoint(sketch, "E250.visualSharp", {"position": v(-37.3, 50.58) * mm});
            skArc(sketch, "E250.filletArc", {"start": v(-37.2, 50.83) * mm, "mid": v(-37.2, 50.63) * mm, "end": v(-37.04, 50.5) * mm});
            skPoint(sketch, "E251.visualSharp", {"position": v(-32.14, 47.95) * mm});
            skArc(sketch, "E251.filletArc", {"start": v(-31.85, 48.64) * mm, "mid": v(-31.85, 48.07) * mm, "end": v(-31.45, 47.66) * mm});
            skPoint(sketch, "E252.visualSharp", {"position": v(-29.46, 54.42) * mm});
            skArc(sketch, "E252.filletArc", {"start": v(-28.77, 54.13) * mm, "mid": v(-29.34, 54.13) * mm, "end": v(-29.75, 53.72) * mm});
            skPoint(sketch, "E253.visualSharp", {"position": v(66.19, 54.25) * mm});
            skArc(sketch, "E253.filletArc", {"start": v(65.93, 54.17) * mm, "mid": v(66.08, 54.3) * mm, "end": v(66.08, 54.5) * mm});
            skPoint(sketch, "E254.visualSharp", {"position": v(68.26, 49.26) * mm});
            skArc(sketch, "E254.filletArc", {"start": v(68.36, 49) * mm, "mid": v(68.22, 49.15) * mm, "end": v(68.01, 49.13) * mm});
            skPoint(sketch, "E255.visualSharp", {"position": v(63.4, 61) * mm});
            skArc(sketch, "E255.filletArc", {"start": v(63.59, 60.53) * mm, "mid": v(63.32, 60.8) * mm, "end": v(62.93, 60.8) * mm});
            skPoint(sketch, "E256.visualSharp", {"position": v(71.05, 42.52) * mm});
            skArc(sketch, "E256.filletArc", {"start": v(70.59, 42.33) * mm, "mid": v(70.86, 42.6) * mm, "end": v(70.86, 42.98) * mm});
            skPoint(sketch, "E257.visualSharp", {"position": v(71.05, 19.82) * mm});
            skArc(sketch, "E257.filletArc", {"start": v(70.86, 19.36) * mm, "mid": v(70.86, 19.74) * mm, "end": v(70.59, 20.01) * mm});
            skPoint(sketch, "E258.visualSharp", {"position": v(63.4, 1.34) * mm});
            skArc(sketch, "E258.filletArc", {"start": v(62.94, 1.53) * mm, "mid": v(63.32, 1.53) * mm, "end": v(63.59, 1.8) * mm});
            skPoint(sketch, "E259.visualSharp", {"position": v(65.31, 5.96) * mm});
            skArc(sketch, "E259.filletArc", {"start": v(65.08, 6.06) * mm, "mid": v(65.27, 6.06) * mm, "end": v(65.4, 6.2) * mm});
            skPoint(sketch, "E260.visualSharp", {"position": v(69.14, 15.2) * mm});
            skArc(sketch, "E260.filletArc", {"start": v(69.04, 14.97) * mm, "mid": v(69.04, 15.16) * mm, "end": v(68.9, 15.3) * mm});
            skPoint(sketch, "E261.visualSharp", {"position": v(68.26, 13.08) * mm});
            skArc(sketch, "E261.filletArc", {"start": v(68.01, 13.2) * mm, "mid": v(68.22, 13.2) * mm, "end": v(68.36, 13.33) * mm});
            skPoint(sketch, "E262.visualSharp", {"position": v(66.19, 8.09) * mm});
            skArc(sketch, "E262.filletArc", {"start": v(66.08, 7.83) * mm, "mid": v(66.08, 8.03) * mm, "end": v(65.93, 8.17) * mm});
            skPoint(sketch, "E263.visualSharp", {"position": v(60.36, 9.64) * mm});
            skArc(sketch, "E263.filletArc", {"start": v(59.67, 9.92) * mm, "mid": v(60.24, 9.92) * mm, "end": v(60.65, 10.33) * mm});
            skPoint(sketch, "E264.visualSharp", {"position": v(63.04, 16.1) * mm});
            skArc(sketch, "E264.filletArc", {"start": v(62.75, 15.4) * mm, "mid": v(62.75, 15.98) * mm, "end": v(62.35, 16.39) * mm});
            skPoint(sketch, "E265.visualSharp", {"position": v(26.03, 23.85) * mm});
            skArc(sketch, "E265.filletArc", {"start": v(27.68, 24.55) * mm, "mid": v(27.22, 23.86) * mm, "end": v(27.68, 23.17) * mm});
            skPoint(sketch, "E266.visualSharp", {"position": v(35.06, 27.7) * mm});
            skArc(sketch, "E266.filletArc", {"start": v(35.44, 27.53) * mm, "mid": v(35.06, 27.6) * mm, "end": v(34.67, 27.53) * mm});
            skPoint(sketch, "E267.visualSharp", {"position": v(8.37, 31.17) * mm});
            skArc(sketch, "E267.filletArc", {"start": v(10.05, 31.86) * mm, "mid": v(9.58, 31.17) * mm, "end": v(10.05, 30.48) * mm});
            skPoint(sketch, "E268.visualSharp", {"position": v(26.64, 31.18) * mm});
            skArc(sketch, "E268.filletArc", {"start": v(25, 30.48) * mm, "mid": v(25.45, 31.17) * mm, "end": v(25, 31.86) * mm});
            skPoint(sketch, "E269.visualSharp", {"position": v(26.01, 38.48) * mm});
            skArc(sketch, "E269.filletArc", {"start": v(27.68, 39.17) * mm, "mid": v(27.22, 38.48) * mm, "end": v(27.68, 37.78) * mm});
            skPoint(sketch, "E270.visualSharp", {"position": v(9.03, 23.86) * mm});
            skArc(sketch, "E270.filletArc", {"start": v(7.35, 23.17) * mm, "mid": v(7.82, 23.86) * mm, "end": v(7.35, 24.56) * mm});
            skPoint(sketch, "E271.visualSharp", {"position": v(-29.46, 7.92) * mm});
            skArc(sketch, "E271.filletArc", {"start": v(-29.75, 8.61) * mm, "mid": v(-29.34, 8.2) * mm, "end": v(-28.77, 8.2) * mm});
            skPoint(sketch, "E272.visualSharp", {"position": v(-32.14, 14.39) * mm});
            skArc(sketch, "E272.filletArc", {"start": v(-31.45, 14.68) * mm, "mid": v(-31.85, 14.27) * mm, "end": v(-31.85, 13.7) * mm});
            skPoint(sketch, "E273.visualSharp", {"position": v(-37.3, 11.76) * mm});
            skArc(sketch, "E273.filletArc", {"start": v(-37.04, 11.84) * mm, "mid": v(-37.2, 11.7) * mm, "end": v(-37.2, 11.5) * mm});
            skPoint(sketch, "E274.visualSharp", {"position": v(-34.97, 6.13) * mm});
            skArc(sketch, "E274.filletArc", {"start": v(-35.08, 6.38) * mm, "mid": v(-34.93, 6.24) * mm, "end": v(-34.73, 6.26) * mm});
            skPoint(sketch, "E275.visualSharp", {"position": v(-36.01, 19.82) * mm});
            skArc(sketch, "E275.filletArc", {"start": v(-35.55, 20.01) * mm, "mid": v(-35.82, 19.74) * mm, "end": v(-35.82, 19.36) * mm});
            skPoint(sketch, "E276.visualSharp", {"position": v(-28.36, 1.34) * mm});
            skArc(sketch, "E276.filletArc", {"start": v(-28.55, 1.8) * mm, "mid": v(-28.28, 1.53) * mm, "end": v(-27.9, 1.53) * mm});
            skPoint(sketch, "E277.visualSharp", {"position": v(-0.12, 27.65) * mm});
            skArc(sketch, "E277.filletArc", {"start": v(0.26, 27.5) * mm, "mid": v(-0.12, 27.57) * mm, "end": v(-0.5, 27.5) * mm});
            skPoint(sketch, "E278.visualSharp", {"position": v(17.62, 27.34) * mm});
            skArc(sketch, "E278.filletArc", {"start": v(17.23, 27.5) * mm, "mid": v(17.62, 27.42) * mm, "end": v(18, 27.5) * mm});
            skPoint(sketch, "E279.visualSharp", {"position": v(17.52, 34.96) * mm});
            skArc(sketch, "E279.filletArc", {"start": v(17.9, 34.8) * mm, "mid": v(17.52, 34.88) * mm, "end": v(17.14, 34.8) * mm});
            skPoint(sketch, "E280.visualSharp", {"position": v(35.25, 34.65) * mm});
            skArc(sketch, "E280.filletArc", {"start": v(34.87, 34.8) * mm, "mid": v(35.25, 34.73) * mm, "end": v(35.64, 34.8) * mm});
            skPoint(sketch, "E281.visualSharp", {"position": v(60.36, 52.7) * mm});
            skArc(sketch, "E281.filletArc", {"start": v(60.65, 52.01) * mm, "mid": v(60.24, 52.42) * mm, "end": v(59.67, 52.42) * mm});
            skPoint(sketch, "E282.visualSharp", {"position": v(63.07, 46.17) * mm});
            skArc(sketch, "E282.filletArc", {"start": v(62.38, 45.88) * mm, "mid": v(62.78, 46.29) * mm, "end": v(62.78, 46.86) * mm});
            skPoint(sketch, "E283.visualSharp", {"position": v(-0.02, 34.65) * mm});
            skArc(sketch, "E283.filletArc", {"start": v(-0.4, 34.8) * mm, "mid": v(-0.02, 34.73) * mm, "end": v(0.36, 34.8) * mm});
            skPoint(sketch, "E284.visualSharp", {"position": v(9.12, 38.44) * mm});
            skArc(sketch, "E284.filletArc", {"start": v(7.45, 37.74) * mm, "mid": v(7.91, 38.44) * mm, "end": v(7.45, 39.13) * mm});
            skPoint(sketch, "E285.visualSharp", {"position": v(65.3, 56.38) * mm});
            skArc(sketch, "E285.filletArc", {"start": v(65.4, 56.15) * mm, "mid": v(65.27, 56.28) * mm, "end": v(65.08, 56.28) * mm});
            skSolve(sketch);
        }
        {
            var Q0;
            Q0=makeQuery(id+"F0.imprint","IMPRINT",FACE,{"disambiguationData":[TD([[makeQuery(id+"F0.imprint","IMPRINT",EDGE,{"derivedFrom":sQuery(id+"F0.wireOp",EDGE,"E41.bottom")}),-1.0]])]});
            var Q1;
            Q1=makeQuery(id+"F0.imprint","IMPRINT",FACE,{"disambiguationData":[TD([[makeQuery(id+"F0.imprint","IMPRINT",EDGE,{"derivedFrom":sQuery(id+"F0.wireOp",EDGE,"E1.bottom")}),-1.0]])]});
            var Q2;
            Q2=makeQuery(id+"F0.imprint","IMPRINT",FACE,{"disambiguationData":[TD([[makeQuery(id+"F0.imprint","IMPRINT",EDGE,{"derivedFrom":sQuery(id+"F0.wireOp",EDGE,"E20.bottom")}),-1.0]])]});
            var Q3;
            Q3=makeQuery(id+"F0.imprint","IMPRINT",FACE,{"disambiguationData":[TD([[makeQuery(id+"F0.imprint","IMPRINT",EDGE,{"derivedFrom":sQuery(id+"F0.wireOp",EDGE,"E53.trimOffspring")}),1.0]])]});
            var Q4;
            Q4=makeQuery(id+"F0.imprint","IMPRINT",FACE,{"disambiguationData":[TD([[makeQuery(id+"F0.imprint","IMPRINT",EDGE,{"derivedFrom":sQuery(id+"F0.wireOp",EDGE,"E20.right")}),-1.0]])]});
            var Q5;
            Q5=makeQuery(id+"F0.imprint","IMPRINT",FACE,{"disambiguationData":[TD([[makeQuery(id+"F0.imprint","IMPRINT",EDGE,{"derivedFrom":sQuery(id+"F0.wireOp",EDGE,"E41.right")}),-1.0]])]});
            var Q6;
            Q6=makeQuery(id+"F0.imprint","IMPRINT",FACE,{"disambiguationData":[TD([[makeQuery(id+"F0.imprint","IMPRINT",EDGE,{"derivedFrom":sQuery(id+"F0.wireOp",EDGE,"dff330fa-bad5-45d3-8442-31bf8b21b129.bottom")}),-1.0]])]});
            var Q7;
            Q7=makeQuery(id+"F0.imprint","IMPRINT",FACE,{"disambiguationData":[TD([[makeQuery(id+"F0.imprint","IMPRINT",EDGE,{"derivedFrom":sQuery(id+"F0.wireOp",EDGE,"4c039687-4170-454c-9726-e4aa64996560.bottom")}),-1.0]])]});
            var Q8;
            Q8=makeQuery(id+"F0.imprint","IMPRINT",FACE,{"disambiguationData":[TD([[makeQuery(id+"F0.imprint","IMPRINT",EDGE,{"derivedFrom":sQuery(id+"F0.wireOp",EDGE,"44739f55-406d-41c5-8a95-b3d1dc047acb.trimOffspring")}),1.0]])]});
            var Q9;
            Q9=makeQuery(id+"F0.imprint","IMPRINT",FACE,{"disambiguationData":[TD([[makeQuery(id+"F0.imprint","IMPRINT",EDGE,{"derivedFrom":sQuery(id+"F0.wireOp",EDGE,"dff330fa-bad5-45d3-8442-31bf8b21b129.right")}),-1.0]])]});
            var Q10;
            Q10=makeQuery(id+"F0.imprint","IMPRINT",FACE,{"disambiguationData":[TD([[makeQuery(id+"F0.imprint","IMPRINT",EDGE,{"derivedFrom":sQuery(id+"F0.wireOp",EDGE,"4c039687-4170-454c-9726-e4aa64996560.right")}),-1.0]])]});
            var Q11;
            Q11=makeQuery(id+"F0.imprint","IMPRINT",FACE,{"disambiguationData":[TD([[makeQuery(id+"F0.imprint","IMPRINT",EDGE,{"derivedFrom":sQuery(id+"F0.wireOp",EDGE,"c4d6db2a-c7ea-4625-92c0-c08ff310b56f.bottom")}),-1.0]])]});
            var Q12;
            Q12=makeQuery(id+"F0.imprint","IMPRINT",FACE,{"disambiguationData":[TD([[makeQuery(id+"F0.imprint","IMPRINT",EDGE,{"derivedFrom":sQuery(id+"F0.wireOp",EDGE,"E144.bottom")}),-1.0]])]});
            var Q13;
            Q13=makeQuery(id+"F0.imprint","IMPRINT",FACE,{"disambiguationData":[TD([[makeQuery(id+"F0.imprint","IMPRINT",EDGE,{"derivedFrom":sQuery(id+"F0.wireOp",EDGE,"E184.bottom")}),-1.0]])]});
            var Q14;
            Q14=makeQuery(id+"F0.imprint","IMPRINT",FACE,{"disambiguationData":[TD([[makeQuery(id+"F0.imprint","IMPRINT",EDGE,{"derivedFrom":sQuery(id+"F0.wireOp",EDGE,"E196.trimOffspring")}),1.0]])]});
            var Q15;
            Q15=makeQuery(id+"F0.imprint","IMPRINT",FACE,{"disambiguationData":[TD([[makeQuery(id+"F0.imprint","IMPRINT",EDGE,{"derivedFrom":sQuery(id+"F0.wireOp",EDGE,"E163.right")}),-1.0]])]});
            var Q16;
            Q16=makeQuery(id+"F0.imprint","IMPRINT",FACE,{"disambiguationData":[TD([[makeQuery(id+"F0.imprint","IMPRINT",EDGE,{"derivedFrom":sQuery(id+"F0.wireOp",EDGE,"E184.right")}),-1.0]])]});
            var Q17;
            Q17=makeQuery(id+"F0.imprint","IMPRINT",FACE,{"disambiguationData":[TD([[makeQuery(id+"F0.imprint","IMPRINT",EDGE,{"derivedFrom":sQuery(id+"F0.wireOp",EDGE,"E163.bottom")}),-1.0]])]});
            extrude(context, id + "F1", {"entities" : qUnion([Q0, Q1, Q2, Q3, Q4, Q5, Q6, Q7, Q8, Q9, Q10, Q11, Q12, Q13, Q14, Q15, Q16, Q17]), "depth" : 0.8 * mm, "offsetDistance" : 25 * mm});
        }
        {
            var Q0;
            Q0=makeQuery(id+"F0.imprint","IMPRINT",FACE,{"disambiguationData":[TD([[makeQuery(id+"F0.imprint","IMPRINT",EDGE,{"derivedFrom":sQuery(id+"F0.wireOp",EDGE,"E21.left")}),1.0]])]});
            var Q1;
            Q1=makeQuery(id+"F0.imprint","IMPRINT",FACE,{"disambiguationData":[TD([[makeQuery(id+"F0.imprint","IMPRINT",EDGE,{"derivedFrom":sQuery(id+"F0.wireOp",EDGE,"E0.bottom")}),-1.0]])]});
            var Q2;
            Q2=makeQuery(id+"F0.imprint","IMPRINT",FACE,{"disambiguationData":[TD([[makeQuery(id+"F0.imprint","IMPRINT",EDGE,{"derivedFrom":sQuery(id+"F0.wireOp",EDGE,"E0.left")}),1.0]])]});
            var Q3;
            Q3=makeQuery(id+"F0.imprint","IMPRINT",FACE,{"disambiguationData":[TD([[makeQuery(id+"F0.imprint","IMPRINT",EDGE,{"derivedFrom":sQuery(id+"F0.wireOp",EDGE,"E0.top")}),1.0]])]});
            var Q4;
            Q4=makeQuery(id+"F0.imprint","IMPRINT",FACE,{"disambiguationData":[TD([[makeQuery(id+"F0.imprint","IMPRINT",EDGE,{"derivedFrom":sQuery(id+"F0.wireOp",EDGE,"E32")}),1.0]])]});
            var Q5;
            Q5=makeQuery(id+"F0.imprint","IMPRINT",FACE,{"disambiguationData":[TD([[makeQuery(id+"F0.imprint","IMPRINT",EDGE,{"derivedFrom":sQuery(id+"F0.wireOp",EDGE,"E22.right")}),1.0]])]});
            var Q6;
            Q6=makeQuery(id+"F0.imprint","IMPRINT",FACE,{"disambiguationData":[TD([[makeQuery(id+"F0.imprint","IMPRINT",EDGE,{"derivedFrom":sQuery(id+"F0.wireOp",EDGE,"E11")}),1.0]])]});
            var Q7;
            Q7=makeQuery(id+"F0.imprint","IMPRINT",FACE,{"disambiguationData":[TD([[makeQuery(id+"F0.imprint","IMPRINT",EDGE,{"derivedFrom":sQuery(id+"F0.wireOp",EDGE,"E53.trimOffspring")}),-1.0]])]});
            var Q8;
            Q8=makeQuery(id+"F0.imprint","IMPRINT",FACE,{"disambiguationData":[TD([[makeQuery(id+"F0.imprint","IMPRINT",EDGE,{"derivedFrom":sQuery(id+"F0.wireOp",EDGE,"E1.right")}),1.0]])]});
            var Q9;
            Q9=makeQuery(id+"F0.imprint","IMPRINT",FACE,{"disambiguationData":[TD([[makeQuery(id+"F0.imprint","IMPRINT",EDGE,{"derivedFrom":sQuery(id+"F0.wireOp",EDGE,"576545d2-502d-470f-84d2-17f3c086c75c.bottom")}),1.0]])]});
            var Q10;
            Q10=makeQuery(id+"F0.imprint","IMPRINT",FACE,{"disambiguationData":[TD([[makeQuery(id+"F0.imprint","IMPRINT",EDGE,{"derivedFrom":sQuery(id+"F0.wireOp",EDGE,"b125ed64-3624-4404-be17-10b159a05513.left")}),1.0]])]});
            var Q11;
            Q11=makeQuery(id+"F0.imprint","IMPRINT",FACE,{"disambiguationData":[TD([[makeQuery(id+"F0.imprint","IMPRINT",EDGE,{"derivedFrom":sQuery(id+"F0.wireOp",EDGE,"2072eac1-4d4c-4828-9e0d-e9294ddb5040")}),1.0]])]});
            var Q12;
            Q12=makeQuery(id+"F0.imprint","IMPRINT",FACE,{"disambiguationData":[TD([[makeQuery(id+"F0.imprint","IMPRINT",EDGE,{"derivedFrom":sQuery(id+"F0.wireOp",EDGE,"9f5e1b98-3d93-4009-9a62-072c4a44ba38.right")}),1.0]])]});
            var Q13;
            Q13=makeQuery(id+"F0.imprint","IMPRINT",FACE,{"disambiguationData":[TD([[makeQuery(id+"F0.imprint","IMPRINT",EDGE,{"derivedFrom":sQuery(id+"F0.wireOp",EDGE,"44739f55-406d-41c5-8a95-b3d1dc047acb.trimOffspring")}),-1.0]])]});
            var Q14;
            Q14=makeQuery(id+"F0.imprint","IMPRINT",FACE,{"disambiguationData":[TD([[makeQuery(id+"F0.imprint","IMPRINT",EDGE,{"derivedFrom":sQuery(id+"F0.wireOp",EDGE,"78cd7a66-e63f-4346-8376-cf85115e82d0.top")}),-1.0]])]});
            var Q15;
            Q15=makeQuery(id+"F0.imprint","IMPRINT",FACE,{"disambiguationData":[TD([[makeQuery(id+"F0.imprint","IMPRINT",EDGE,{"derivedFrom":sQuery(id+"F0.wireOp",EDGE,"7f6f85a7-f928-4766-b9e2-5d4449b1a277.left")}),1.0]])]});
            var Q16;
            Q16=makeQuery(id+"F0.imprint","IMPRINT",FACE,{"disambiguationData":[TD([[makeQuery(id+"F0.imprint","IMPRINT",EDGE,{"derivedFrom":sQuery(id+"F0.wireOp",EDGE,"5ace8697-f47f-403b-886a-c3eafd523042")}),1.0]])]});
            var Q17;
            Q17=makeQuery(id+"F0.imprint","IMPRINT",FACE,{"disambiguationData":[TD([[makeQuery(id+"F0.imprint","IMPRINT",EDGE,{"derivedFrom":sQuery(id+"F0.wireOp",EDGE,"78cd7a66-e63f-4346-8376-cf85115e82d0.right")}),1.0]])]});
            var Q18;
            Q18=makeQuery(id+"F0.imprint","IMPRINT",FACE,{"disambiguationData":[TD([[makeQuery(id+"F0.imprint","IMPRINT",EDGE,{"derivedFrom":sQuery(id+"F0.wireOp",EDGE,"E143.left")}),1.0]])]});
            var Q19;
            Q19=makeQuery(id+"F0.imprint","IMPRINT",FACE,{"disambiguationData":[TD([[makeQuery(id+"F0.imprint","IMPRINT",EDGE,{"derivedFrom":sQuery(id+"F0.wireOp",EDGE,"E143.bottom")}),-1.0]])]});
            var Q20;
            Q20=makeQuery(id+"F0.imprint","IMPRINT",FACE,{"disambiguationData":[TD([[makeQuery(id+"F0.imprint","IMPRINT",EDGE,{"derivedFrom":sQuery(id+"F0.wireOp",EDGE,"E143.top")}),1.0]])]});
            var Q21;
            Q21=makeQuery(id+"F0.imprint","IMPRINT",FACE,{"disambiguationData":[TD([[makeQuery(id+"F0.imprint","IMPRINT",EDGE,{"derivedFrom":sQuery(id+"F0.wireOp",EDGE,"E196.trimOffspring")}),-1.0]])]});
            var Q22;
            Q22=makeQuery(id+"F0.imprint","IMPRINT",FACE,{"disambiguationData":[TD([[makeQuery(id+"F0.imprint","IMPRINT",EDGE,{"derivedFrom":sQuery(id+"F0.wireOp",EDGE,"E175")}),1.0]])]});
            var Q23;
            Q23=makeQuery(id+"F0.imprint","IMPRINT",FACE,{"disambiguationData":[TD([[makeQuery(id+"F0.imprint","IMPRINT",EDGE,{"derivedFrom":sQuery(id+"F0.wireOp",EDGE,"E154")}),1.0]])]});
            var Q24;
            Q24=makeQuery(id+"F0.imprint","IMPRINT",FACE,{"disambiguationData":[TD([[makeQuery(id+"F0.imprint","IMPRINT",EDGE,{"derivedFrom":sQuery(id+"F0.wireOp",EDGE,"E165.right")}),1.0]])]});
            var Q25;
            Q25=makeQuery(id+"F0.imprint","IMPRINT",FACE,{"disambiguationData":[TD([[makeQuery(id+"F0.imprint","IMPRINT",EDGE,{"derivedFrom":sQuery(id+"F0.wireOp",EDGE,"E144.right")}),1.0]])]});
            var Q26;
            Q26=makeQuery(id+"F0.imprint","IMPRINT",FACE,{"disambiguationData":[TD([[makeQuery(id+"F0.imprint","IMPRINT",EDGE,{"derivedFrom":sQuery(id+"F0.wireOp",EDGE,"E164.left")}),1.0]])]});
            extrude(context, id + "F2", {"entities" : qUnion([Q0, Q1, Q2, Q3, Q4, Q5, Q6, Q7, Q8, Q9, Q10, Q11, Q12, Q13, Q14, Q15, Q16, Q17, Q18, Q19, Q20, Q21, Q22, Q23, Q24, Q25, Q26]), "depth" : 2 * mm, "offsetDistance" : 25 * mm});
        }
    });
